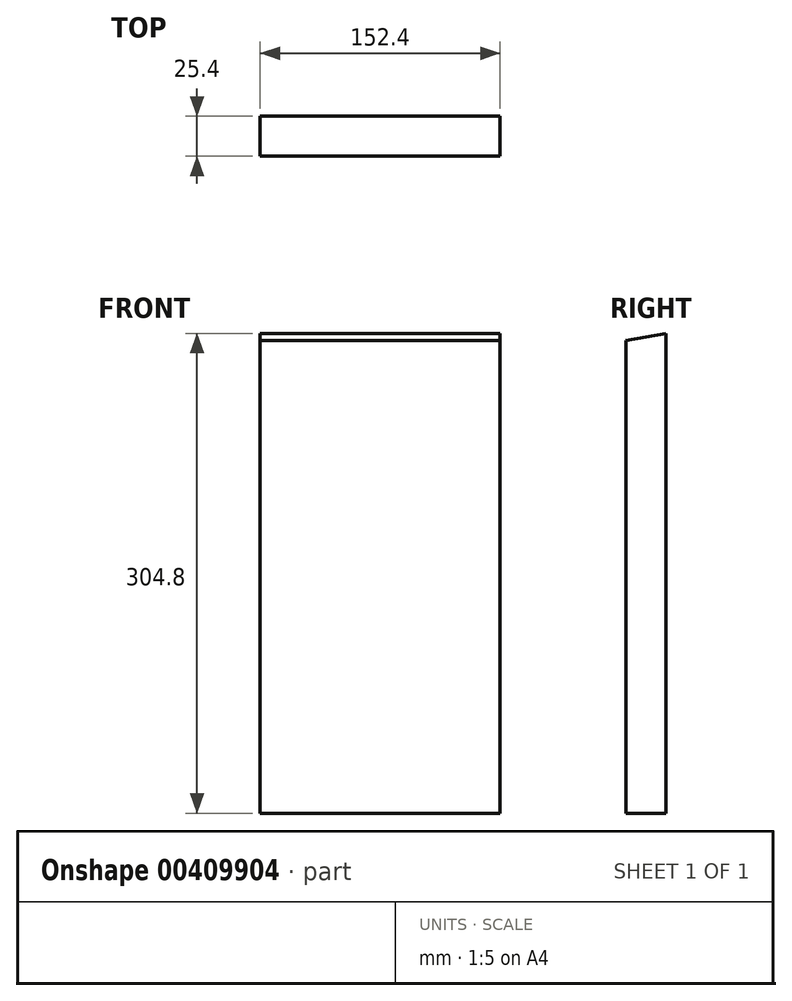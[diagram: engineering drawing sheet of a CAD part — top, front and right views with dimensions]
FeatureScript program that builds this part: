
annotation { "Feature Type Name" : "Feature", "Feature Type Description" : "" }
export const myFeature = defineFeature(function(context is Context, id is Id, definition is map)
    precondition{}
    {
        {
            var Q0;
            Q0=qCreatedBy(makeId("Front.planeOp"),FACE);
            var sketch = newSketch(context, id + "F0", { "sketchPlane" : qUnion([Q0])});
            skLineSegment(sketch, "E0.bottom", {"start": v(-77.74, 178.51) * mm, "end": v(74.66, 178.51) * mm});
            skLineSegment(sketch, "E0.top", {"start": v(-77.74, -126.29) * mm, "end": v(74.66, -126.29) * mm});
            skLineSegment(sketch, "E0.left", {"start": v(-77.74, 178.51) * mm, "end": v(-77.74, -126.29) * mm});
            skLineSegment(sketch, "E0.right", {"start": v(74.66, 178.51) * mm, "end": v(74.66, -126.29) * mm});
            skSolve(sketch);
        }
        {
            var Q0;
            Q0=makeQuery(id+"F0.imprint","IMPRINT",FACE,{"disambiguationData":[TD([[makeQuery(id+"F0.imprint","IMPRINT",EDGE,{"derivedFrom":sQuery(id+"F0.wireOp",EDGE,"E0.bottom")}),-1.0]])]});
            extrude(context, id + "F1", {"entities" : qUnion([Q0]), "depth" : 25.4 * mm});
        }
        {
            var Q0;
            Q0=makeQuery(id+"F1.opExtrude","CAP_EDGE",EDGE,{"disambiguationData":[OSD([sQuery(id+"F0.wireOp",EDGE,"E0.bottom")])],"isStart":false});
            chamfer(context, id + "F2", {"entities" : qUnion([Q0]), "chamferType" : ChamferType.OFFSET_ANGLE, "width" : 25.4 * mm, "oppositeDirection" : false, "angle" : 10 * degree, "tangentPropagation" : true});
        }
    });
